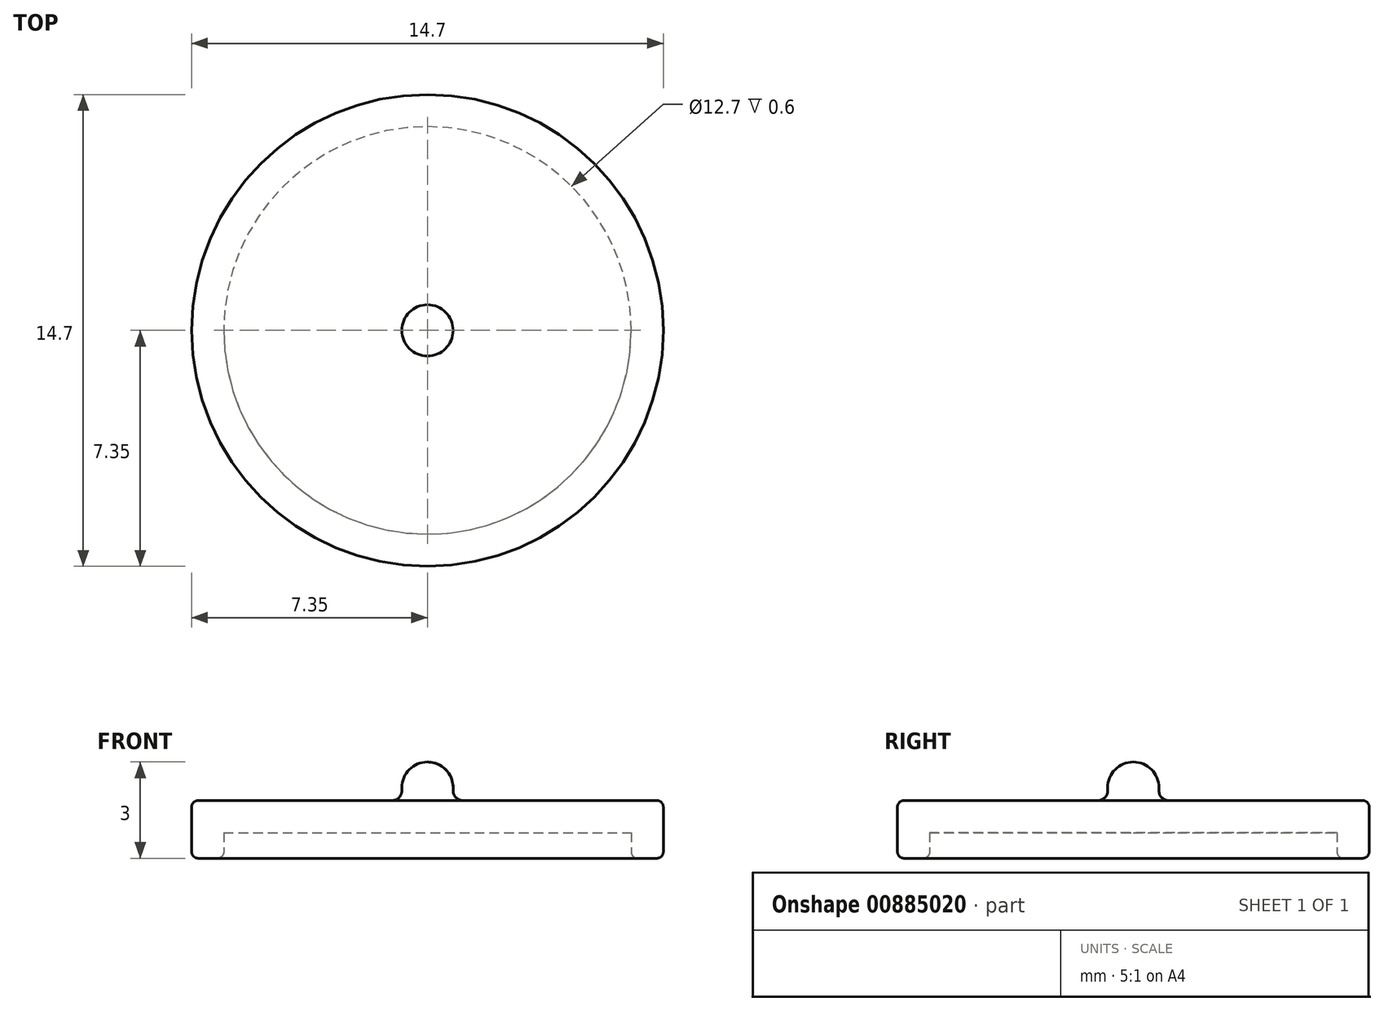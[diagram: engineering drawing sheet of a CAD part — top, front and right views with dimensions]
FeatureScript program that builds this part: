
annotation { "Feature Type Name" : "Feature", "Feature Type Description" : "" }
export const myFeature = defineFeature(function(context is Context, id is Id, definition is map)
    precondition{}
    {
        {
            var Q0;
            Q0=qCreatedBy(makeId("Front.planeOp"),FACE);
            var sketch = newSketch(context, id + "F0", { "sketchPlane" : qUnion([Q0])});
            skLineSegment(sketch, "E0", {"start": v(0, 0) * mm, "end": v(0, 1) * mm});
            skLineSegment(sketch, "E1", {"start": v(0, 1) * mm, "end": v(-7.35, 1) * mm});
            skLineSegment(sketch, "E2", {"start": v(-7.35, 1) * mm, "end": v(-7.35, -0.8) * mm});
            skLineSegment(sketch, "E3", {"start": v(-7.35, -0.8) * mm, "end": v(-6.35, -0.8) * mm});
            skLineSegment(sketch, "E4", {"start": v(-6.35, -0.8) * mm, "end": v(-6.35, 0) * mm});
            skLineSegment(sketch, "E5", {"start": v(-6.35, 0) * mm, "end": v(0, 0) * mm});
            skLineSegment(sketch, "E6.bottom", {"start": v(0, 1) * mm, "end": v(-0.8, 1) * mm});
            skLineSegment(sketch, "E6.top", {"start": v(0, 1.4) * mm, "end": v(-0.8, 1.4) * mm});
            skLineSegment(sketch, "E6.left", {"start": v(0, 1) * mm, "end": v(0, 1.4) * mm});
            skLineSegment(sketch, "E6.right", {"start": v(-0.8, 1) * mm, "end": v(-0.8, 1.4) * mm});
            skArc(sketch, "E7", {"start": v(-0.8, 1.4) * mm, "mid": v(-0.57, 1.97) * mm, "end": v(0, 2.2) * mm});
            skLineSegment(sketch, "E8", {"start": v(0, 2.2) * mm, "end": v(0, 1.4) * mm});
            skSolve(sketch);
        }
        {
            var Q0;
            {var subQ2=sQuery(id+"F0.wireOp",EDGE,"E0");Q0=makeQuery(id+"F0.imprint","IMPRINT",FACE,{"disambiguationData":[TD([[makeQuery(id+"F0.imprint","IMPRINT",EDGE,{"derivedFrom":subQ2}),1.0]])]});}
            var Q1;
            {var subQ0=sQuery(id+"F0.wireOp",EDGE,"wYFL7p8j-TeGG-kjCM-6JJ2-xih8vC0nYGVt");Q1=makeQuery(id+"F0.imprint","IMPRINT",FACE,{"disambiguationData":[TD([[makeQuery(id+"F0.imprint","IMPRINT",EDGE,{"derivedFrom":subQ0}),1.0]])]});}
            var Q2;
            Q2=makeQuery(id+"F0.imprint","IMPRINT",FACE,{"disambiguationData":[TD([[makeQuery(id+"F0.imprint","IMPRINT",EDGE,{"derivedFrom":sQuery(id+"F0.wireOp",EDGE,"E6.top")}),1.0]])]});
            var Q3;
            Q3=makeQuery(id+"F0.imprint","IMPRINT",FACE,{"disambiguationData":[TD([[makeQuery(id+"F0.imprint","IMPRINT",EDGE,{"derivedFrom":sQuery(id+"F0.wireOp",EDGE,"E6.top")}),-1.0]])]});
            var Q4;
            Q4=sQuery(id+"F0.wireOp",EDGE,"E0");
            revolve(context, id + "F1", {"entities" : qUnion([Q0, Q1, Q2, Q3]), "axis" : qUnion([Q4]), "revolveType" : RevolveType.FULL, "surfaceOperationType" : NewSurfaceOperationType.NEW});
        }
        {
            var Q0;
            Q0=makeQuery(id+"F1.opRevolve","SWEPT_EDGE",EDGE,{"disambiguationData":[OSD([sQuery(id+"F0.wireOp",EDGE,"E1"),sQuery(id+"F0.wireOp",EDGE,"E2")])]});
            var Q1;
            Q1=makeQuery(id+"F1.opRevolve","SWEPT_EDGE",EDGE,{"disambiguationData":[OSD([sQuery(id+"F0.wireOp",EDGE,"E2"),sQuery(id+"F0.wireOp",EDGE,"E3")])]});
            var Q2;
            Q2=makeQuery(id+"F1.opRevolve","SWEPT_EDGE",EDGE,{"disambiguationData":[OSD([sQuery(id+"F0.wireOp",EDGE,"E3"),sQuery(id+"F0.wireOp",EDGE,"E4")])]});
            fillet(context, id + "F2", {"entities" : qUnion([Q0, Q1, Q2]), "radius" : 0.2 * mm, "tangentPropagation" : true, "allowEdgeOverflow" : false});
        }
        {
            var Q0;
            Q0=makeQuery(id+"F1.opRevolve","SWEPT_EDGE",EDGE,{"disambiguationData":[OSD([sQuery(id+"F0.wireOp",EDGE,"E1"),sQuery(id+"F0.wireOp",EDGE,"E6.right")])]});
            fillet(context, id + "F3", {"entities" : qUnion([Q0]), "radius" : 0.3 * mm, "tangentPropagation" : true, "allowEdgeOverflow" : false});
        }
    });
